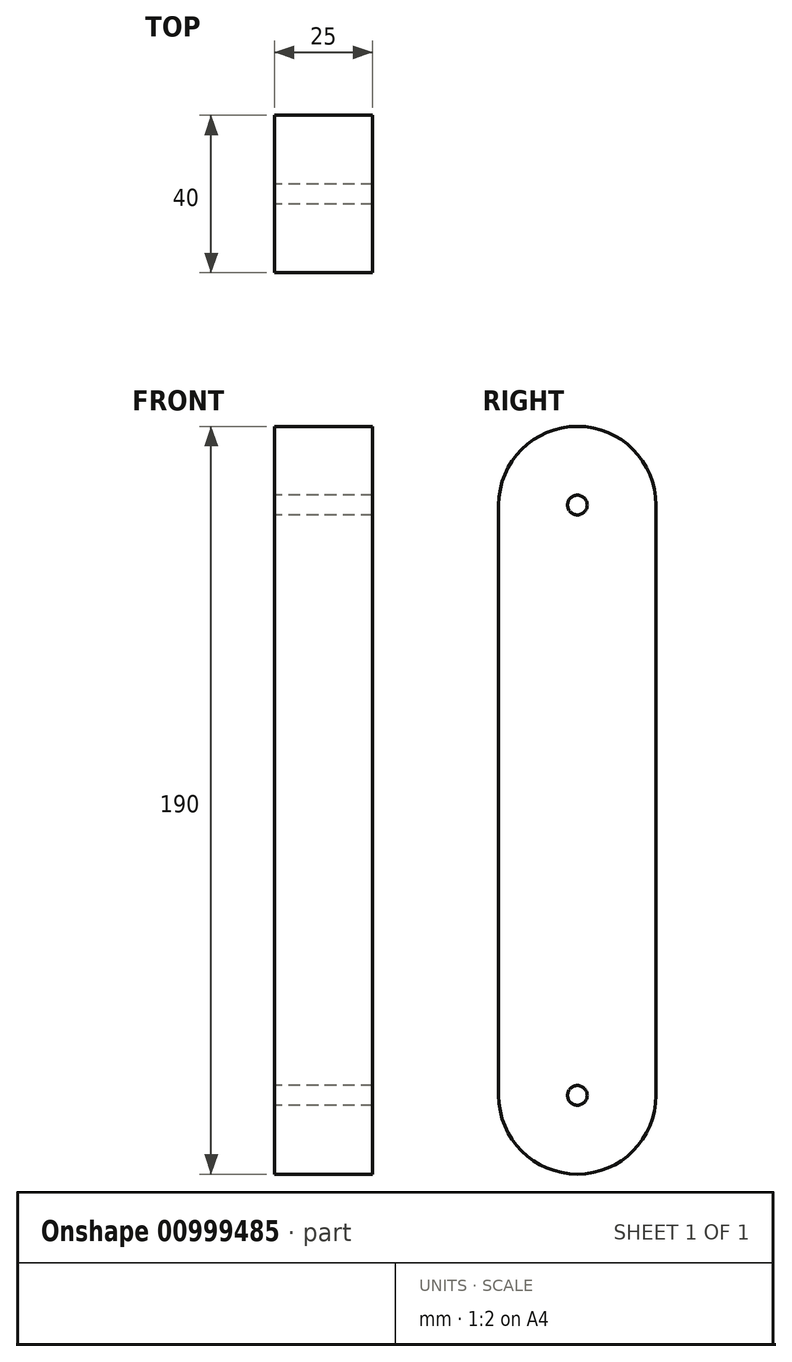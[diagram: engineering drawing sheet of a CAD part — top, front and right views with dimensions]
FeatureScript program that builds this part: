
annotation { "Feature Type Name" : "Feature", "Feature Type Description" : "" }
export const myFeature = defineFeature(function(context is Context, id is Id, definition is map)
    precondition{}
    {
        {
            var Q0;
            Q0=qCreatedBy(makeId("Right.planeOp"),FACE);
            var sketch = newSketch(context, id + "F0", { "sketchPlane" : qUnion([Q0])});
            skLineSegment(sketch, "E0", {"start": v(0, 0) * mm, "end": v(0, 150) * mm});
            skLineSegment(sketch, "E1", {"start": v(40.24, 0) * mm, "end": v(40.24, 150) * mm});
            skArc(sketch, "E2", {"start": v(0, 0) * mm, "mid": v(20, -20) * mm, "end": v(40, 0) * mm});
            skArc(sketch, "E3", {"start": v(40, 150) * mm, "mid": v(20, 170) * mm, "end": v(0, 150) * mm});
            skCircle(sketch, "E4", {"center": v(20, 0) * mm, "radius": 2.5 * mm});
            skCircle(sketch, "E5", {"center": v(20, 150) * mm, "radius": 2.5 * mm});
            skLineSegment(sketch, "E6", {"start": v(40, 150) * mm, "end": v(40, 0) * mm});
            skSolve(sketch);
        }
        {
            var Q0;
            Q0=makeQuery(id+"F0.imprint","IMPRINT",FACE,{"disambiguationData":[TD([[makeQuery(id+"F0.imprint","IMPRINT",EDGE,{"derivedFrom":sQuery(id+"F0.wireOp",EDGE,"E0")}),-1.0]])]});
            extrude(context, id + "F1", {"entities" : qUnion([Q0]), "depth" : 25 * mm, "offsetDistance" : 25 * mm});
        }
        {
            var Q0;
            Q0=sQuery(id+"F0.wireOp",EDGE,"E4");
            extrude(context, id + "F2", {"bodyType" : ToolBodyType.SURFACE, "surfaceEntities" : qUnion([Q0]), "oppositeDirection" : true, "depth" : 46 * mm, "offsetDistance" : 25 * mm});
        }
    });
